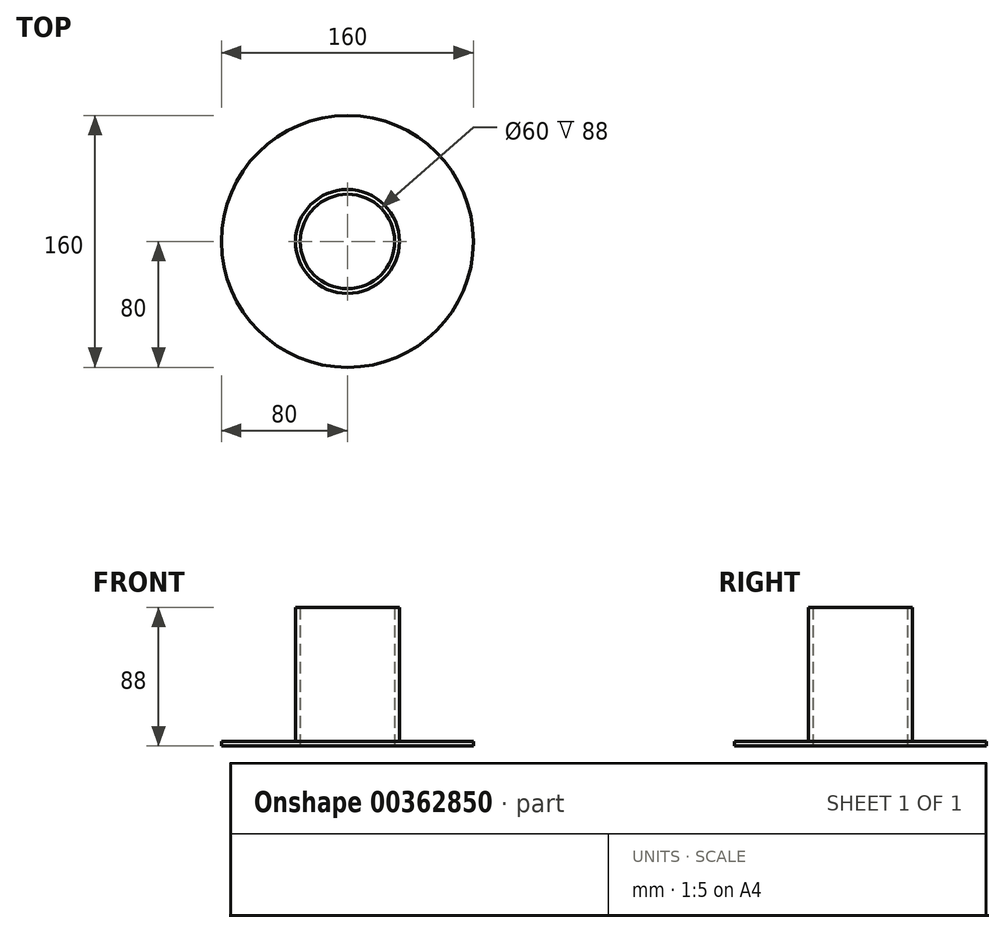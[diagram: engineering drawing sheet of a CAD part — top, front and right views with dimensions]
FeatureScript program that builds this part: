
annotation { "Feature Type Name" : "Feature", "Feature Type Description" : "" }
export const myFeature = defineFeature(function(context is Context, id is Id, definition is map)
    precondition{}
    {
        {
            var Q0;
            Q0=qCreatedBy(makeId("Top.planeOp"),FACE);
            var sketch = newSketch(context, id + "F0", { "sketchPlane" : qUnion([Q0])});
            skCircle(sketch, "E0", {"center": v(0, 0) * mm, "radius": 30 * mm});
            skCircle(sketch, "E1", {"center": v(0, 0) * mm, "radius": 80 * mm});
            skSolve(sketch);
        }
        {
            var Q0;
            Q0 = qSketchRegion(id + "F0", true);
            extrude(context, id + "F1", {"entities" : qUnion([Q0]), "depth" : 3 * mm});
        }
        {
            var Q0;
            Q0=makeQuery(id+"F1.opExtrude","CAP_FACE",FACE,{"disambiguationData":[OSD([sQuery(id+"F0.wireOp",EDGE,"E0"),sQuery(id+"F0.wireOp",EDGE,"E1")])],"isStart":false});
            var sketch = newSketch(context, id + "F2", { "sketchPlane" : qUnion([Q0])});
            skCircle(sketch, "E2.0", {"center": v(0, 0) * mm, "radius": 30 * mm});
            skCircle(sketch, "E3.0", {"center": v(0, 0) * mm, "radius": 33 * mm});
            skSolve(sketch);
        }
        {
            var Q0;
            Q0 = qSketchRegion(id + "F2", true);
            var Q1;
            Q1=sQuery(id+"F2.wireOp",EDGE,"E3.0");
            extrude(context, id + "F3", {"entities" : qUnion([Q0]), "operationType" : NewBodyOperationType.ADD, "surfaceEntities" : qUnion([Q1]), "depth" : 85 * mm});
        }
    });
